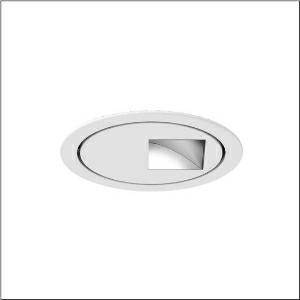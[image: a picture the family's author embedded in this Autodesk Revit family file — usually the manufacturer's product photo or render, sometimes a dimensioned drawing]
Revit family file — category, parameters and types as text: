
# Revit family: lunis_11_mini_round_51dk11cd2wf21
name_source: partatom
category: Lighting Fixtures
units: mm (PartAtom-declared; Revit-internal decimal feet)

## family parameters
Cut with Voids When Loaded = No
Host = Face
Light Source = No
Part Type = Normal
Room Calculation Point = No
Round Connector Dimension = Use Diameter
Shared = No

## types (1)
- Lunis 11 mini round (1 x LED 3000K / CRI = 80 (unbekannt), 2380 lm, 3000K)
    Apparent Load = 28 VA
    CIE Flux Codes = 44 77 97 100 100
    Color Rendering = 80
    Color Temperature = 3000K
    Default Elevation = 1800 mm
    Description = Lunis 11 mini round, downlight, light control with wallwasher, of highly reflective aluminium, highly specular, light emission: direct distribution, LED rated luminous flux: 2.380lm, light colour: 830, control gear: ECG, with terminal, 5-pole, mains connection: 220..230V, AC/DC, 0/50..60Hz, LED module, luminaire module, of aluminium, highly specular, white, diameter: 176mm, clamping range: 1..40mm, recessing ring, of plastic, traffic white (RAL 9016), protection rating (complete): IP20, insulation class (complete): insulation class II (safety insulation), certification: CE, permissible ambient temperature for indoor applications: 0..+35°C, packaging unit: 1 piece
    Height = 0 mm  [stored 0 ft]
    Lamp = 1 x LED 3000K / CRI >= 80 (unbekannt)
    Lamp Light Flux = 2380 lm
    Lamp count = 1
    Length = 176 mm
    Luminous efficacy = 86 lm/W
    Manufacturer = Siteco
    ModVariant = No
    Model = 51DK11CD2WF21
    Mounting Place = Ceiling
    Mounting Type = Recessed
    Number of Poles = 1
    OnlyDefault = Yes
    Power Factor = 1
    Product Name = Lunis 11 mini round
    Product group = downlight
    ProductGroupID = 401
    Protection Class = Protection class II
    Protection Degree = IP 20
    RLX_Detail_Level = 1
    RLX_Emergency_Light_Flux = 0 lm
    RLX_Emergency_Type = 0
    RLX_Emergency_Type_DB = No
    RlxData = <blob elided: 59361 chars, md5=87edd82a>
    Socket = socket
    Standby Power = 0 W
    System Light Flux = 2380 lm
    System Power = 28 W
    Type Comments = Product without accessories
    Type Image = l_1004772.jpg
    URL = http://relux.com
    VarID = ---
    Voltage = 0 V
    Weight = 0.00 kg
    Width = 176 mm

note: [stored X ft] marks values corroborated as IEEE doubles in the binary element streams (Revit-internal decimal feet)

## geometry (parser evidence)
native form markers: Blend x4, Sweep x12
no freeform markers — native parametric forms only
